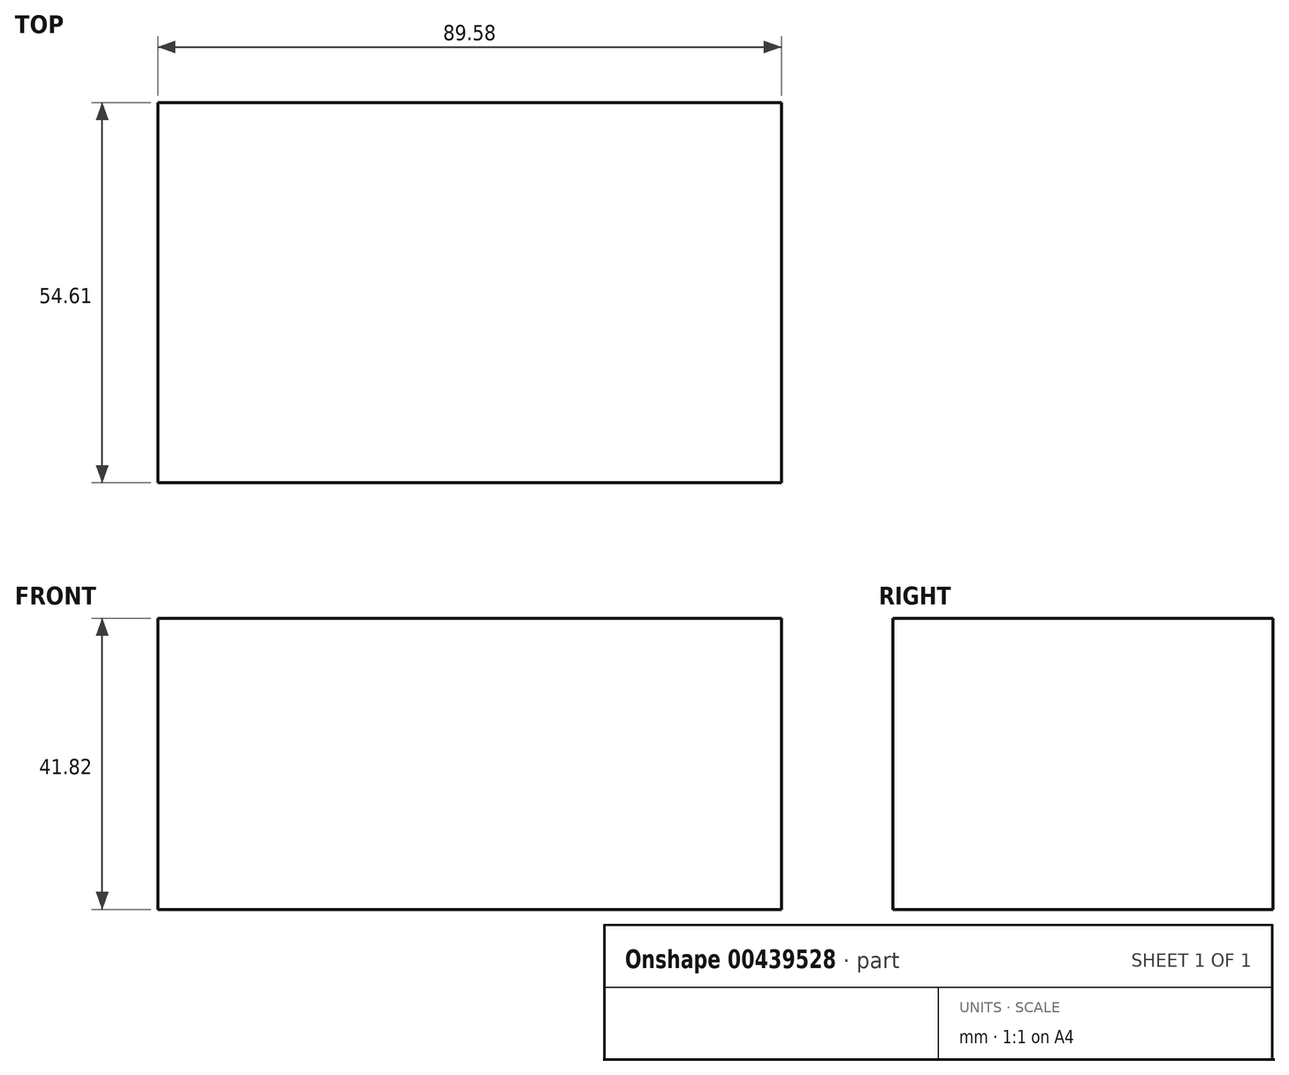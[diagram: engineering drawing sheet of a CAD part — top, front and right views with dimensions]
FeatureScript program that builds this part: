
annotation { "Feature Type Name" : "Feature", "Feature Type Description" : "" }
export const myFeature = defineFeature(function(context is Context, id is Id, definition is map)
    precondition{}
    {
        {
            var Q0;
            Q0=qCreatedBy(makeId("Front.planeOp"),FACE);
            var sketch = newSketch(context, id + "F0", { "sketchPlane" : qUnion([Q0])});
            skLineSegment(sketch, "E0.bottom", {"start": v(44.79, -12.3) * mm, "end": v(-44.79, -12.3) * mm});
            skLineSegment(sketch, "E0.top", {"start": v(44.79, 29.52) * mm, "end": v(-44.79, 29.52) * mm});
            skLineSegment(sketch, "E0.left", {"start": v(44.79, -12.3) * mm, "end": v(44.79, 29.52) * mm});
            skLineSegment(sketch, "E0.right", {"start": v(-44.79, -12.3) * mm, "end": v(-44.79, 29.52) * mm});
            skPoint(sketch, "E0.middle", {"position": v(0, 8.61) * mm});
            skSolve(sketch);
        }
        {
            var Q0;
            Q0=makeQuery(id+"F0.imprint","IMPRINT",FACE,{"disambiguationData":[TD([[makeQuery(id+"F0.imprint","IMPRINT",EDGE,{"derivedFrom":sQuery(id+"F0.wireOp",EDGE,"E0.bottom")}),-1.0]])]});
            extrude(context, id + "F1", {"entities" : qUnion([Q0]), "depth" : 54.6 * mm});
        }
    });
